FCSTD DOCUMENT  (FreeCAD 2023.521R14555 (Git shallow))
Label: asm
License: All rights reserved
objects: App::Link×6, App::DocumentObjectGroup×3, PartDesign::CoordinateSystem×1, App::FeaturePython×1, App::Part×1
note: 1 computed .brp shape members not serialized (recipe doc carries the construction recipe); baked Part::Feature solids carry a one-line shape summary decoded from their .brp
EXTERNAL_REF file=Main_board.FCStd obj=Local_CS
EXTERNAL_REF file=Main_board.FCStd obj=Part
EXTERNAL_REF file=Main_board.FCStd obj=Local_CS002
EXTERNAL_REF file=Triangle.FCStd obj=LCS_0
EXTERNAL_REF file=Triangle.FCStd obj=Triangle
EXTERNAL_REF file=Circle.FCStd obj=Local_CS
EXTERNAL_REF file=Main_board.FCStd obj=Local_CS003
EXTERNAL_REF file=Circle.FCStd obj=Part
EXTERNAL_REF file=Main_board.FCStd obj=Local_CS004
EXTERNAL_REF file=Penta.FCStd obj=LCS_0
EXTERNAL_REF file=Penta.FCStd obj=Penta
EXTERNAL_REF file=Hex.FCStd obj=Local_CS001
EXTERNAL_REF file=Main_board.FCStd obj=Local_CS005
EXTERNAL_REF file=Hex.FCStd obj=Hex

FEATURE [App::Link] Part  label="Part(Part)"
  AttachedBy = #Local_CS
  AttachedTo = Parent Assembly#LCS_Origin
  AutoLinkLabel = true
  AutoPlacement = true
  LinkPlacement = pos=(40,-40,-4) rot=(-1,0,0;1.5708rad)
  LinkedObject = -> <external Main_board.FCStd>#Part
  Placement = pos=(40,-40,-4) rot=(-1,0,0;1.5708rad)
  SolverId = Asm4EE
  SyncGroupVisibility = false
  TreeRank = 19
  _LinkVersion = 1
  expr: Placement = LCS_Origin.Placement * AttachmentOffset * Main_board#Local_CS.Placement ^ (-1)
FEATURE [App::DocumentObjectGroup] Parts
  ClaimAllChildren = true
  ExportMode = 1
  TreeRank = 22
  _GroupVersion = 1
FEATURE [PartDesign::CoordinateSystem] LCS_Origin
  AttacherType = Attacher::AttachEngine3D
  AttachmentSupport = -> [X_Axis]
  InvalidShape = false
  MapMode = 2
  Support = -> [X_Axis]
  TreeRank = 4
  ValidateShape = false
FEATURE [App::DocumentObjectGroup] Constraints
  ClaimAllChildren = true
  ExportMode = 1
  TreeRank = 11
  _GroupVersion = 1
FEATURE [App::FeaturePython] Variables  # WARN: FeaturePython — macro-defined, semantics opaque (R4)
  TreeRank = 17
  Type = App::PropertyContainer
FEATURE [App::DocumentObjectGroup] Configurations
  ClaimAllChildren = true
  ExportMode = 1
  TreeRank = 18
  _GroupVersion = 1
FEATURE [App::Link] Triangle  label="Triangle(Triangle)"
  AttachedBy = #LCS_0
  AttachedTo = Part#Local_CS002
  AttachmentOffset = pos=(0,0,0) rot=(1,0,0;1.5708rad)
  AutoLinkLabel = true
  AutoPlacement = true
  LinkPlacement = pos=(80,-80,0) rot=(0,0.707107,0.707107;3.14159rad)
  LinkedObject = -> <external Triangle.FCStd>#Triangle
  Placement = pos=(80,-80,0) rot=(0,0.707107,0.707107;3.14159rad)
  SolverId = Asm4EE
  SyncGroupVisibility = false
  TreeRank = 24
  _LinkVersion = 1
  expr: Placement = Part.Placement * Main_board#Local_CS002.Placement * AttachmentOffset * Triangle#LCS_0.Placement ^ (-1)
FEATURE [App::Link] Triangle001  label="Triangle"
  AttachedBy = #LCS_0
  AttachedTo = Part#Local_CS
  AttachmentOffset = pos=(0,0,0) rot=(1,0,0;1.5708rad)
  AutoLinkLabel = true
  AutoPlacement = true
  LinkPlacement = pos=(0,0,0) rot=(1,0,0;1.5708rad)
  LinkedObject = -> <external Triangle.FCStd>#Triangle
  Placement = pos=(0,0,0) rot=(1,0,0;1.5708rad)
  SolverId = Asm4EE
  SyncGroupVisibility = false
  TreeRank = 25
  _LinkVersion = 1
  expr: Placement = Part.Placement * Main_board#Local_CS.Placement * AttachmentOffset * Triangle#LCS_0.Placement ^ (-1)
FEATURE [App::Link] Circle  label="Circle(Circle)"
  AttachedBy = #Local_CS
  AttachedTo = Part#Local_CS003
  AutoLinkLabel = true
  AutoPlacement = true
  LinkPlacement = pos=(40,-40,-10) rot=(-0.57735,-0.57735,0.57735;2.0944rad)
  LinkedObject = -> <external Circle.FCStd>#Part
  Placement = pos=(40,-40,-10) rot=(-0.57735,-0.57735,0.57735;2.0944rad)
  SolverId = Asm4EE
  SyncGroupVisibility = false
  TreeRank = 26
  _LinkVersion = 1
  expr: Placement = Part.Placement * Main_board#Local_CS003.Placement * AttachmentOffset * Circle#Local_CS.Placement ^ (-1)
FEATURE [App::Link] Penta  label="Penta(Penta)"
  AttachedBy = #LCS_0
  AttachedTo = Part#Local_CS004
  AttachmentOffset = pos=(0,0,0) rot=(0.57735,0.57735,0.57735;2.0944rad)
  AutoLinkLabel = true
  AutoPlacement = true
  LinkPlacement = pos=(80,-8.9244e-12,0) rot=(0,-0.707107,-0.707107;3.14159rad)
  LinkedObject = -> <external Penta.FCStd>#Penta
  Placement = pos=(80,-8.9244e-12,0) rot=(0,-0.707107,-0.707107;3.14159rad)
  SolverId = Asm4EE
  SyncGroupVisibility = false
  TreeRank = 27
  _LinkVersion = 1
  expr: Placement = Part.Placement * Main_board#Local_CS004.Placement * AttachmentOffset * Penta#LCS_0.Placement ^ (-1)
FEATURE [App::Link] Hex  label="Hex(Hex)"
  AttachedBy = #Local_CS001
  AttachedTo = Part#Local_CS005
  AttachmentOffset = pos=(0,0,0) rot=(0,0,1;4.71239rad)
  AutoLinkLabel = true
  AutoPlacement = true
  LinkPlacement = pos=(4.3912e-12,-80,0) rot=(0,-0.707107,-0.707107;3.14159rad)
  LinkedObject = -> <external Hex.FCStd>#Hex
  Placement = pos=(4.3912e-12,-80,0) rot=(0,-0.707107,-0.707107;3.14159rad)
  SolverId = Asm4EE
  SyncGroupVisibility = false
  TreeRank = 28
  _LinkVersion = 1
  expr: Placement = Part.Placement * Main_board#Local_CS005.Placement * AttachmentOffset * Hex#Local_CS001.Placement ^ (-1)
FEATURE [App::Part] Assembly
  AssemblyType = Part::Link
  ClaimAllChildren = false
  ExportMode = 1
  Group = -> [LCS_Origin,Constraints,Variables,Configurations,Part,Triangle,Triangle001,Circle,Penta,Hex]
  Origin = -> Origin
  TreeRank = 23
  Type = Assembly
  _ExportChildren = -> [LCS_Origin,Constraints,Variables,Configurations,Part,Triangle,Triangle001,Circle,Penta,Hex]
  _GroupVersion = 1

RESOLVED EXTERNAL PARTS (link-assembly join: the EXTERNAL_REF files above that resolve inside this repo's crawl, each included once):
---- part Circle.FCStd = doc fcstd_3b26a44b2be2 ----
FCSTD DOCUMENT  (FreeCAD 2023.521R14555 (Git shallow))
Label: Circle
License: All rights reserved
objects: Sketcher::SketchObject×1, PartDesign::Pad×1, PartDesign::Body×1, PartDesign::CoordinateSystem×1, App::Part×1, App::Link×1
note: 7 computed .brp shape members not serialized (recipe doc carries the construction recipe); baked Part::Feature solids carry a one-line shape summary decoded from their .brp
EXTERNAL_REF file=Main_board.FCStd obj=Spreadsheet

FEATURE [Sketcher::SketchObject] Sketch
  ArcFitTolerance = 1e-06
  AttachmentSupport = -> [XZ_Plane]
  ExternalBSplineMaxDegree = 5
  ExternalBSplineTolerance = 0.0001
  FullyConstrained = true
  InternalTolerance = 1e-06
  InvalidShape = false
  MakeInternals = false
  MapMode = 5
  Placement = pos=(0,0,0) rot=(1,0,0;1.5708rad)
  Support = -> [XZ_Plane]
  TreeRank = 14
  ValidateShape = false
  expr: Constraints[1] = <<dims>>.PS
  sketch-geometry (1):
    g0: Circle CenterX=0 CenterY=0 CenterZ=0 NormalX=0 NormalY=0 NormalZ=1 AngleXU=0 Radius=20
  constraints (2):
    c: Coincident(g0,g-1)
    c: Diameter(g0) = 40
FEATURE [PartDesign::Pad] Pad
  AddSubType = 0
  AlongSketchNormal = false
  AutoTaperInnerAngle = true
  CheckUpToFaceLimits = true
  ClaimChildren = false
  Direction = (0,-1,-2e-16)
  Fit = 0
  FitJoin = 0
  InnerFit = 0
  InnerFitJoin = 0
  InvalidShape = false
  Length = 10
  Length2 = 10
  Linearize = true
  NewSolid = false
  Profile = -> Sketch
  ReferenceAxis = -> Sketch [N_Axis]
  Suppress = false
  TaperInnerAngle = 0
  TaperInnerAngleRev = 0
  TreeRank = 15
  Type = 0
  ValidateShape = true
  _ProfileBasedVersion = 1
FEATURE [PartDesign::Body] Body
  AutoGroupSolids = false
  ClaimAllChildren = false
  ExportMode = 0
  Group = -> [Sketch,Pad]
  InvalidShape = false
  Origin = -> Origin001
  Tip = -> Pad
  TreeRank = 13
  ValidateShape = false
  _ExportChildren = -> [Pad]
  _GroupVersion = 1
FEATURE [PartDesign::CoordinateSystem] Local_CS
  AttacherType = Attacher::AttachEngine3D
  AttachmentSupport = -> [Pad]
  InvalidShape = false
  MapMode = 5
  Placement = pos=(0,-10,-2.2e-15) rot=(1,0,0;1.5708rad)
  Support = -> [Pad]
  TreeRank = 16
  ValidateShape = false
FEATURE [App::Part] Part  label="Circle"
  ClaimAllChildren = false
  ExportMode = 1
  Group = -> [Body,Local_CS]
  Origin = -> Origin
  TreeRank = 3
  _ExportChildren = -> [Body,Local_CS]
  _GroupVersion = 1
FEATURE [App::Link] Link  label="dims"
  AutoLinkLabel = true
  AutoPlacement = true
  LinkedObject = -> <external Main_board.FCStd>#Spreadsheet
  SyncGroupVisibility = false
  TreeRank = 17
  _LinkVersion = 1
---- part Hex.FCStd = doc fcstd_f15830a4f873 ----
FCSTD DOCUMENT  (FreeCAD 2023.521R14555 (Git shallow))
Label: Hex
License: All rights reserved
objects: Sketcher::SketchObject×1, PartDesign::Pad×1, PartDesign::Body×1, App::Link×1, PartDesign::CoordinateSystem×1, App::Part×1
note: 7 computed .brp shape members not serialized (recipe doc carries the construction recipe); baked Part::Feature solids carry a one-line shape summary decoded from their .brp
EXTERNAL_REF file=Main_board.FCStd obj=Spreadsheet

FEATURE [Sketcher::SketchObject] Sketch
  ArcFitTolerance = 1e-06
  AttachmentSupport = -> [XZ_Plane001]
  ExternalBSplineMaxDegree = 5
  ExternalBSplineTolerance = 0.0001
  FullyConstrained = true
  InternalTolerance = 1e-06
  InvalidShape = false
  MakeInternals = false
  MapMode = 5
  Placement = pos=(0,0,0) rot=(1,0,0;1.5708rad)
  Support = -> [XZ_Plane001]
  TreeRank = 23
  ValidateShape = false
  expr: Constraints[18] = <<dims>>.PS
  sketch-geometry (7):
    g0: LineSegment StartX=-17.3205 StartY=10 StartZ=0 EndX=-17.3205 EndY=-10 EndZ=0
    g1: LineSegment StartX=-17.3205 StartY=-10 StartZ=0 EndX=3.6e-15 EndY=-20 EndZ=0
    g2: LineSegment StartX=2.1e-15 StartY=-20 StartZ=0 EndX=17.3205 EndY=-10 EndZ=0
    g3: LineSegment StartX=17.3205 StartY=-10 StartZ=0 EndX=17.3205 EndY=10 EndZ=0
    g4: LineSegment StartX=17.3205 StartY=10 StartZ=0 EndX=0 EndY=20 EndZ=0
    g5: LineSegment StartX=2e-16 StartY=20 StartZ=0 EndX=-17.3205 EndY=10 EndZ=0
    g6: Circle [constr] CenterX=0 CenterY=0 CenterZ=0 NormalX=0 NormalY=0 NormalZ=1 AngleXU=0 Radius=20
  constraints (16):
    c: Coincident(g0,g1)
    c: Coincident(g1,g2)
    c: Coincident(g2,g3)
    c: Coincident(g3,g4)
    c: Coincident(g4,g5)
    c: Coincident(g5,g0)
    c: Equal(g0, g1-g5) x5
    c: PointOnObject(g0,g6)
    c: PointOnObject(g1,g6)
    c: PointOnObject(g2,g6)
    c: PointOnObject(g3,g6)
    c: PointOnObject(g4,g6)
    c: PointOnObject(g5,g6)
    c: Coincident(g6,g-1)
    c: Diameter(g6) = 40
    c: Vertical(g3)
FEATURE [PartDesign::Pad] Pad
  AddSubType = 0
  AlongSketchNormal = false
  AutoTaperInnerAngle = true
  CheckUpToFaceLimits = true
  ClaimChildren = false
  Direction = (0,-1,-2e-16)
  Fit = 0
  FitJoin = 0
  InnerFit = 0
  InnerFitJoin = 0
  InvalidShape = false
  Length = 10
  Length2 = 10
  Linearize = true
  NewSolid = false
  Profile = -> Sketch
  ReferenceAxis = -> Sketch [N_Axis]
  Suppress = false
  TaperInnerAngle = 0
  TaperInnerAngleRev = 0
  TreeRank = 24
  Type = 0
  ValidateShape = true
  _ProfileBasedVersion = 1
FEATURE [PartDesign::Body] Body
  AutoGroupSolids = false
  ClaimAllChildren = false
  ExportMode = 0
  Group = -> [Sketch,Pad]
  InvalidShape = false
  Origin = -> Origin001
  Tip = -> Pad
  TreeRank = 22
  ValidateShape = false
  _ExportChildren = -> [Pad]
  _GroupVersion = 1
FEATURE [App::Link] Link  label="dims"
  AutoLinkLabel = true
  AutoPlacement = true
  LinkedObject = -> <external Main_board.FCStd>#Spreadsheet
  SyncGroupVisibility = false
  TreeRank = 26
  _LinkVersion = 1
FEATURE [PartDesign::CoordinateSystem] Local_CS001
  AttacherType = Attacher::AttachEngine3D
  AttachmentSupport = -> [XZ_Plane]
  InvalidShape = false
  MapMode = 5
  Placement = pos=(0,0,0) rot=(0,0.707107,0.707107;3.14159rad)
  Support = -> [XZ_Plane]
  TreeRank = 30
  ValidateShape = false
FEATURE [App::Part] Hex
  ClaimAllChildren = false
  ExportMode = 1
  Group = -> [Body,Local_CS001]
  Origin = -> Origin
  TreeRank = 11
  _ExportChildren = -> [Body,Local_CS001]
  _GroupVersion = 1
---- part Main_board.FCStd = doc fcstd_18a85a5c1fb4 ----
FCSTD DOCUMENT  (FreeCAD 2023.521R14555 (Git shallow))
Label: Main_board
License: All rights reserved
objects: PartDesign::CoordinateSystem×5, Sketcher::SketchObject×2, PartDesign::Pad×1, Spreadsheet::Sheet×1, PartDesign::Body×1, App::Part×1
note: 13 computed .brp shape members not serialized (recipe doc carries the construction recipe); baked Part::Feature solids carry a one-line shape summary decoded from their .brp

FEATURE [Sketcher::SketchObject] Sketch
  ArcFitTolerance = 1e-06
  AttachmentSupport = -> [XZ_Plane]
  ExternalBSplineMaxDegree = 5
  ExternalBSplineTolerance = 0.0001
  FullyConstrained = true
  InternalTolerance = 1e-06
  InvalidShape = false
  MakeInternals = false
  MapMode = 5
  Placement = pos=(0,0,0) rot=(1,0,0;1.5708rad)
  Support = -> [XZ_Plane]
  TreeRank = 11
  ValidateShape = false
  expr: Constraints[48] = <<dims>>.HS
  sketch-geometry (31):
    g0: LineSegment StartX=-40 StartY=19 StartZ=0 EndX=-21.8135 EndY=50.5 EndZ=0
    g1: LineSegment StartX=-21.8135 StartY=50.5 StartZ=0 EndX=-58.1865 EndY=50.5 EndZ=0
    g2: LineSegment StartX=-58.1865 StartY=50.5 StartZ=0 EndX=-40 EndY=19 EndZ=0
    g3: Circle [constr] CenterX=-40 CenterY=40 CenterZ=0 NormalX=0 NormalY=0 NormalZ=1 AngleXU=0 Radius=21
    g4: LineSegment StartX=40 StartY=-19 StartZ=0 EndX=21.8135 EndY=-50.5 EndZ=0
    g5: LineSegment StartX=21.8135 StartY=-50.5 StartZ=0 EndX=58.1865 EndY=-50.5 EndZ=0
    g6: LineSegment StartX=58.1865 StartY=-50.5 StartZ=0 EndX=40 EndY=-19 EndZ=0
    g7: Circle [constr] CenterX=40 CenterY=-40 CenterZ=0 NormalX=0 NormalY=0 NormalZ=1 AngleXU=0 Radius=21
    g8: LineSegment StartX=27.6565 StartY=23.0106 StartZ=0 EndX=52.3435 EndY=23.0106 EndZ=0
    g9: LineSegment StartX=52.3435 StartY=23.0106 StartZ=0 EndX=59.9722 EndY=46.4894 EndZ=0
    g10: LineSegment StartX=59.9722 StartY=46.4894 StartZ=0 EndX=40 EndY=61 EndZ=0
    g11: LineSegment StartX=40 StartY=61 StartZ=0 EndX=20.0278 EndY=46.4894 EndZ=0
    g12: LineSegment StartX=20.0278 StartY=46.4894 StartZ=0 EndX=27.6565 EndY=23.0106 EndZ=0
    g13: Circle [constr] CenterX=40 CenterY=40 CenterZ=0 NormalX=0 NormalY=0 NormalZ=1 AngleXU=0 Radius=21
    g14: LineSegment StartX=-21.8135 StartY=-29.5 StartZ=0 EndX=-40 EndY=-19 EndZ=0
    g15: LineSegment StartX=-40 StartY=-19 StartZ=0 EndX=-58.1865 EndY=-29.5 EndZ=0
    g16: LineSegment StartX=-58.1865 StartY=-29.5 StartZ=0 EndX=-58.1865 EndY=-50.5 EndZ=0
    g17: LineSegment StartX=-58.1865 StartY=-50.5 StartZ=0 EndX=-40 EndY=-61 EndZ=0
    g18: LineSegment StartX=-40 StartY=-61 StartZ=0 EndX=-21.8135 EndY=-50.5 EndZ=0
    g19: LineSegment StartX=-21.8135 StartY=-50.5 StartZ=0 EndX=-21.8135 EndY=-29.5 EndZ=0
    g20: Circle [constr] CenterX=-40 CenterY=-40 CenterZ=0 NormalX=0 NormalY=0 NormalZ=1 AngleXU=0 Radius=21
    g21: Circle CenterX=0 CenterY=0 CenterZ=0 NormalX=0 NormalY=0 NormalZ=1 AngleXU=0 Radius=21
    g22: LineSegment [constr] StartX=-40 StartY=40 StartZ=0 EndX=40 EndY=40 EndZ=0
    g23: LineSegment [constr] StartX=40 StartY=40 StartZ=0 EndX=40 EndY=-40 EndZ=0
    g24: LineSegment [constr] StartX=40 StartY=-40 StartZ=0 EndX=-40 EndY=-40 EndZ=0
    g25: LineSegment [constr] StartX=-40 StartY=-40 StartZ=0 EndX=-40 EndY=40 EndZ=0
    g26: LineSegment StartX=-70 StartY=-70 StartZ=0 EndX=-70 EndY=70 EndZ=0
    g27: LineSegment StartX=-70 StartY=70 StartZ=0 EndX=70 EndY=70 EndZ=0
    g28: LineSegment StartX=70 StartY=70 StartZ=0 EndX=70 EndY=-70 EndZ=0
    g29: LineSegment StartX=70 StartY=-70 StartZ=0 EndX=-70 EndY=-70 EndZ=0
    g30: GeomPoint [constr] X=0 Y=0 Z=0
  constraints (77):
    c: Coincident(g0,g1)
    c: Coincident(g1,g2)
    c: Coincident(g2,g0)
    c: Equal(g0,g1)
    c: Equal(g0,g2)
    c: PointOnObject(g0,g3)
    c: PointOnObject(g1,g3)
    c: PointOnObject(g2,g3)
    c: Coincident(g4,g5)
    c: Coincident(g5,g6)
    c: Coincident(g6,g4)
    c: Equal(g4,g5)
    c: Equal(g4,g6)
    c: PointOnObject(g4,g7)
    c: PointOnObject(g5,g7)
    c: PointOnObject(g6,g7)
    c: Coincident(g8,g9)
    c: Coincident(g9,g10)
    c: Coincident(g10,g11)
    c: Coincident(g11,g12)
    c: Coincident(g12,g8)
    c: Equal(g8, g9-g12) x4
    c: PointOnObject(g8,g13)
    c: PointOnObject(g9,g13)
    c: PointOnObject(g10,g13)
    c: PointOnObject(g11,g13)
    c: PointOnObject(g12,g13)
    c: Coincident(g14,g15)
    c: Coincident(g15,g16)
    c: Coincident(g16,g17)
    c: Coincident(g17,g18)
    c: Coincident(g18,g19)
    c: Coincident(g19,g14)
    c: Equal(g14, g15-g19) x5
    c: PointOnObject(g14,g20)
    c: PointOnObject(g15,g20)
    c: PointOnObject(g16,g20)
    c: PointOnObject(g17,g20)
    c: PointOnObject(g18,g20)
    c: PointOnObject(g19,g20)
    c: Coincident(g21,g-1)
    c: Diameter(g13) = 42
    c: Horizontal(g8)
    c: Equal(g13,g7)
    c: Equal(g7,g20)
    c: Equal(g20,g3)
    c: Vertical(g19)
    c: Horizontal(g5)
    c: Horizontal(g1)
    c: Coincident(g22,g23)
    c: Coincident(g23,g24)
    c: Coincident(g24,g25)
    c: Coincident(g25,g22)
    c: Horizontal(g22)
    c: Horizontal(g24)
    c: Vertical(g23)
    c: Vertical(g25)
    c: Coincident(g22,g3)
    c: Coincident(g23,g7)
    c: Coincident(g22,g13)
    c: Coincident(g24,g20)
    c: Symmetric(g24,g22,g21)
    c: Equal(g23,g24)
    c: DistanceY(g23,g23) = 80
    c: Coincident(g26,g27)
    c: Coincident(g27,g28)
    c: Coincident(g28,g29)
    c: Coincident(g29,g26)
    c: Horizontal(g27)
    c: Horizontal(g29)
    c: Vertical(g26)
    c: Vertical(g28)
    c: Symmetric(g27,g26,g30)
    c: Coincident(g30,g21)
    c: Equal(g28,g29)
    c: DistanceY(g28,g28) = 140
    c: Equal(g21,g13)
FEATURE [PartDesign::Pad] Pad
  AddSubType = 0
  AlongSketchNormal = false
  AutoTaperInnerAngle = true
  CheckUpToFaceLimits = true
  ClaimChildren = false
  Direction = (0,-1,-2e-16)
  Fit = 0
  FitJoin = 0
  InnerFit = 0
  InnerFitJoin = 0
  InvalidShape = false
  Length = 4
  Length2 = 10
  Linearize = true
  NewSolid = false
  Profile = -> Sketch
  ReferenceAxis = -> Sketch [N_Axis]
  Suppress = false
  TaperInnerAngle = 0
  TaperInnerAngleRev = 0
  TreeRank = 12
  Type = 0
  ValidateShape = true
  _ProfileBasedVersion = 1
FEATURE [PartDesign::CoordinateSystem] Local_CS  label="Triangle0"
  AttacherType = Attacher::AttachEngine3D
  AttachmentSupport = -> [Pad]
  InvalidShape = false
  MapMode = 13
  Placement = pos=(-40,-4,40) rot=(1,0,0;1.5708rad)
  Support = -> [Pad]
  TreeRank = 16
  ValidateShape = false
FEATURE [PartDesign::CoordinateSystem] Local_CS002  label="Triangle1"
  AttacherType = Attacher::AttachEngine3D
  AttachmentOffset = pos=(0,0,0) rot=(0,0,1;3.14159rad)
  AttachmentSupport = -> [Pad]
  InvalidShape = false
  MapMode = 13
  Placement = pos=(40,-4,-40) rot=(0,-0.707107,0.707107;3.14159rad)
  Support = -> [Pad]
  TreeRank = 21
  ValidateShape = false
FEATURE [PartDesign::CoordinateSystem] Local_CS003  label="Circle"
  AttacherType = Attacher::AttachEngine3D
  AttachmentSupport = -> [Pad]
  InvalidShape = false
  MapMode = 11
  Placement = pos=(0,-4,-9e-16) rot=(0.57735,-0.57735,0.57735;2.0944rad)
  Support = -> [Pad]
  TreeRank = 22
  ValidateShape = false
FEATURE [Spreadsheet::Sheet] Spreadsheet  label="dims"
  PythonMode = false
  ShowCells = 0
  TreeRank = 25
  cells = A1=Part SIze; B1(PS)==40mm; A2=Gap; B2==2mm; A3=Hole Size; B3(HS)==B1 + B2
FEATURE [Sketcher::SketchObject] Sketch001
  ArcFitTolerance = 1e-06
  AttachmentSupport = -> [Pad]
  ExternalBSplineMaxDegree = 5
  ExternalBSplineTolerance = 0.0001
  ExternalGeometry = -> [Pad]
  FullyConstrained = true
  InternalTolerance = 1e-06
  InvalidShape = false
  MakeInternals = false
  MapMode = 5
  Placement = pos=(0,-4,-9e-16) rot=(1,0,0;1.5708rad)
  Support = -> [Pad]
  TreeRank = 26
  ValidateShape = false
  sketch-geometry (2):
    g0: Circle CenterX=40 CenterY=40 CenterZ=0 NormalX=0 NormalY=0 NormalZ=1 AngleXU=0 Radius=21
    g1: Circle CenterX=-40 CenterY=-40 CenterZ=0 NormalX=0 NormalY=0 NormalZ=1 AngleXU=0 Radius=21
  constraints (6):
    c: PointOnObject(g-4,g0)
    c: PointOnObject(g-3,g0)
    c: PointOnObject(g-3,g0)
    c: PointOnObject(g-5,g1)
    c: PointOnObject(g-6,g1)
    c: PointOnObject(g-6,g1)
FEATURE [PartDesign::Body] Body
  AutoGroupSolids = false
  ClaimAllChildren = false
  ExportMode = 0
  Group = -> [Sketch,Pad,Sketch001]
  InvalidShape = false
  Origin = -> Origin
  Tip = -> Pad
  TreeRank = 10
  ValidateShape = false
  _ExportChildren = -> [Pad,Sketch001]
  _GroupVersion = 1
FEATURE [PartDesign::CoordinateSystem] Local_CS004  label="Penta"
  AttacherType = Attacher::AttachEngine3D
  AttachmentSupport = -> [Sketch001]
  InvalidShape = false
  MapMode = 11
  Placement = pos=(40,-4,40) rot=(-0.57735,0.57735,-0.57735;4.18879rad)
  Support = -> [Sketch001]
  TreeRank = 23
  ValidateShape = false
FEATURE [PartDesign::CoordinateSystem] Local_CS005  label="Hex"
  AttacherType = Attacher::AttachEngine3D
  AttachmentSupport = -> [Sketch001]
  InvalidShape = false
  MapMode = 11
  Placement = pos=(-40,-4,-40) rot=(-0.57735,0.57735,-0.57735;4.18879rad)
  Support = -> [Sketch001]
  TreeRank = 24
  ValidateShape = false
FEATURE [App::Part] Part
  ClaimAllChildren = false
  ExportMode = 1
  Group = -> [Body,Local_CS,Local_CS002,Local_CS003,Local_CS004,Local_CS005]
  Origin = -> Origin001
  TreeRank = 15
  _ExportChildren = -> [Body,Local_CS,Local_CS002,Local_CS003,Local_CS004,Local_CS005]
  _GroupVersion = 1
---- part Penta.FCStd = doc fcstd_dc206007bbaf ----
FCSTD DOCUMENT  (FreeCAD 2023.521R14555 (Git shallow))
Label: Penta
License: All rights reserved
objects: PartDesign::CoordinateSystem×2, Sketcher::SketchObject×1, PartDesign::Pad×1, PartDesign::Body×1, App::Part×1, App::Link×1
note: 8 computed .brp shape members not serialized (recipe doc carries the construction recipe); baked Part::Feature solids carry a one-line shape summary decoded from their .brp
EXTERNAL_REF file=Main_board.FCStd obj=Spreadsheet

FEATURE [PartDesign::CoordinateSystem] LCS_0
  AttacherType = Attacher::AttachEngine3D
  AttachmentSupport = -> [X_Axis]
  InvalidShape = false
  MapMode = 2
  Support = -> [X_Axis]
  TreeRank = 3
  ValidateShape = false
FEATURE [PartDesign::CoordinateSystem] LCS_0001
  AttacherType = Attacher::AttachEngine3D
  AttachmentSupport = -> [X_Axis001]
  InvalidShape = false
  MapMode = 2
  Support = -> [X_Axis001]
  TreeRank = 21
  ValidateShape = false
FEATURE [Sketcher::SketchObject] Sketch
  ArcFitTolerance = 1e-06
  AttachmentSupport = -> [XZ_Plane001]
  ExternalBSplineMaxDegree = 5
  ExternalBSplineTolerance = 0.0001
  FullyConstrained = true
  InternalTolerance = 1e-06
  InvalidShape = false
  MakeInternals = false
  MapMode = 5
  Placement = pos=(0,0,0) rot=(1,0,0;1.5708rad)
  Support = -> [XZ_Plane001]
  TreeRank = 23
  ValidateShape = false
  expr: Constraints[15] = <<dims>>.PS
  sketch-geometry (6):
    g0: LineSegment StartX=3.1e-15 StartY=20 StartZ=0 EndX=-19.0211 EndY=6.18034 EndZ=0
    g1: LineSegment StartX=-19.0211 StartY=6.18034 StartZ=0 EndX=-11.7557 EndY=-16.1803 EndZ=0
    g2: LineSegment StartX=-11.7557 StartY=-16.1803 StartZ=0 EndX=11.7557 EndY=-16.1803 EndZ=0
    g3: LineSegment StartX=11.7557 StartY=-16.1803 StartZ=0 EndX=19.0211 EndY=6.18034 EndZ=0
    g4: LineSegment StartX=19.0211 StartY=6.18034 StartZ=0 EndX=3.6e-15 EndY=20 EndZ=0
    g5: Circle [constr] CenterX=0 CenterY=0 CenterZ=0 NormalX=0 NormalY=0 NormalZ=1 AngleXU=0 Radius=20
  constraints (14):
    c: Coincident(g0,g1)
    c: Coincident(g1,g2)
    c: Coincident(g2,g3)
    c: Coincident(g3,g4)
    c: Coincident(g4,g0)
    c: Equal(g0, g1-g4) x4
    c: PointOnObject(g0,g5)
    c: PointOnObject(g1,g5)
    c: PointOnObject(g2,g5)
    c: PointOnObject(g3,g5)
    c: PointOnObject(g4,g5)
    c: Coincident(g5,g-1)
    c: Diameter(g5) = 40
    c: Horizontal(g2)
FEATURE [PartDesign::Pad] Pad
  AddSubType = 0
  AlongSketchNormal = false
  AutoTaperInnerAngle = true
  CheckUpToFaceLimits = true
  ClaimChildren = false
  Direction = (0,-1,2e-16)
  Fit = 0
  FitJoin = 0
  InnerFit = 0
  InnerFitJoin = 0
  InvalidShape = false
  Length = 10
  Length2 = 10
  Linearize = true
  NewSolid = false
  Profile = -> Sketch
  ReferenceAxis = -> Sketch [N_Axis]
  Suppress = false
  TaperInnerAngle = 0
  TaperInnerAngleRev = 0
  TreeRank = 24
  Type = 0
  ValidateShape = true
  _ProfileBasedVersion = 1
FEATURE [PartDesign::Body] Body
  AutoGroupSolids = false
  ClaimAllChildren = false
  ExportMode = 0
  Group = -> [LCS_0001,Sketch,Pad]
  InvalidShape = false
  Origin = -> Origin001
  Tip = -> Pad
  TreeRank = 22
  ValidateShape = false
  _ExportChildren = -> [LCS_0001,Pad]
  _GroupVersion = 1
FEATURE [App::Part] Penta
  ClaimAllChildren = false
  ExportMode = 1
  Group = -> [LCS_0,Body]
  Origin = -> Origin
  TreeRank = 11
  _ExportChildren = -> [LCS_0,Body]
  _GroupVersion = 1
FEATURE [App::Link] Link  label="dims"
  AutoLinkLabel = true
  AutoPlacement = true
  LinkedObject = -> <external Main_board.FCStd>#Spreadsheet
  SyncGroupVisibility = false
  TreeRank = 26
  _LinkVersion = 1
---- part Triangle.FCStd = doc fcstd_18315d9fd6ea ----
FCSTD DOCUMENT  (FreeCAD 2023.521R14555 (Git shallow))
Label: Triangle
License: All rights reserved
objects: PartDesign::CoordinateSystem×3, Sketcher::SketchObject×1, PartDesign::Pad×1, PartDesign::Body×1, App::Part×1, App::Link×1
note: 9 computed .brp shape members not serialized (recipe doc carries the construction recipe); baked Part::Feature solids carry a one-line shape summary decoded from their .brp
EXTERNAL_REF file=Main_board.FCStd obj=Spreadsheet

FEATURE [PartDesign::CoordinateSystem] LCS_0
  AttacherType = Attacher::AttachEngine3D
  AttachmentSupport = -> [X_Axis]
  InvalidShape = false
  MapMode = 2
  Support = -> [X_Axis]
  TreeRank = 3
  ValidateShape = false
FEATURE [PartDesign::CoordinateSystem] LCS_0001
  AttacherType = Attacher::AttachEngine3D
  AttachmentSupport = -> [X_Axis001]
  InvalidShape = false
  MapMode = 2
  Support = -> [X_Axis001]
  TreeRank = 21
  ValidateShape = false
FEATURE [Sketcher::SketchObject] Sketch
  ArcFitTolerance = 1e-06
  AttachmentSupport = -> [XZ_Plane001]
  ExternalBSplineMaxDegree = 5
  ExternalBSplineTolerance = 0.0001
  FullyConstrained = true
  InternalTolerance = 1e-06
  InvalidShape = false
  MakeInternals = false
  MapMode = 5
  Placement = pos=(0,0,0) rot=(1,0,0;1.5708rad)
  Support = -> [XZ_Plane001]
  TreeRank = 23
  ValidateShape = false
  expr: Constraints[10] = <<dims>>.PS
  sketch-geometry (4):
    g0: LineSegment StartX=17.3205 StartY=-10 StartZ=0 EndX=-7.1e-15 EndY=20 EndZ=0
    g1: LineSegment StartX=-7.8e-15 StartY=20 StartZ=0 EndX=-17.3205 EndY=-10 EndZ=0
    g2: LineSegment StartX=-17.3205 StartY=-10 StartZ=0 EndX=17.3205 EndY=-10 EndZ=0
    g3: Circle [constr] CenterX=0 CenterY=0 CenterZ=0 NormalX=0 NormalY=0 NormalZ=1 AngleXU=0 Radius=20
  constraints (11):
    c: Coincident(g0,g1)
    c: Coincident(g1,g2)
    c: Coincident(g2,g0)
    c: Equal(g0,g1)
    c: Equal(g0,g2)
    c: PointOnObject(g0,g3)
    c: PointOnObject(g1,g3)
    c: PointOnObject(g2,g3)
    c: Coincident(g3,g-1)
    c: Horizontal(g2)
    c: Diameter(g3) = 40
FEATURE [PartDesign::Pad] Pad
  AddSubType = 0
  AlongSketchNormal = false
  AutoTaperInnerAngle = true
  CheckUpToFaceLimits = true
  ClaimChildren = false
  Direction = (0,-1,-2e-16)
  Fit = 0
  FitJoin = 0
  InnerFit = 0
  InnerFitJoin = 0
  InvalidShape = false
  Length = 10
  Length2 = 10
  Linearize = true
  NewSolid = false
  Profile = -> Sketch
  ReferenceAxis = -> Sketch [N_Axis]
  Suppress = false
  TaperInnerAngle = 0
  TaperInnerAngleRev = 0
  TreeRank = 24
  Type = 0
  ValidateShape = true
  _ProfileBasedVersion = 1
FEATURE [PartDesign::CoordinateSystem] Local_CS
  AttacherType = Attacher::AttachEngine3D
  AttachmentSupport = -> [Pad]
  InvalidShape = false
  MapMode = 13
  Placement = pos=(-2.4e-15,-10,-1.66e-14) rot=(1,0,0;1.5708rad)
  Support = -> [Pad]
  TreeRank = 25
  ValidateShape = false
FEATURE [PartDesign::Body] Body
  AutoGroupSolids = false
  ClaimAllChildren = false
  ExportMode = 0
  Group = -> [LCS_0001,Sketch,Pad,Local_CS]
  InvalidShape = false
  Origin = -> Origin001
  Tip = -> Pad
  TreeRank = 22
  ValidateShape = false
  _ExportChildren = -> [LCS_0001,Pad,Local_CS]
  _GroupVersion = 1
FEATURE [App::Part] Triangle
  ClaimAllChildren = false
  ExportMode = 1
  Group = -> [LCS_0,Body]
  Origin = -> Origin
  TreeRank = 11
  _ExportChildren = -> [LCS_0,Body]
  _GroupVersion = 1
FEATURE [App::Link] Link  label="dims"
  AutoLinkLabel = true
  AutoPlacement = true
  LinkedObject = -> <external Main_board.FCStd>#Spreadsheet
  SyncGroupVisibility = false
  TreeRank = 26
  _LinkVersion = 1
